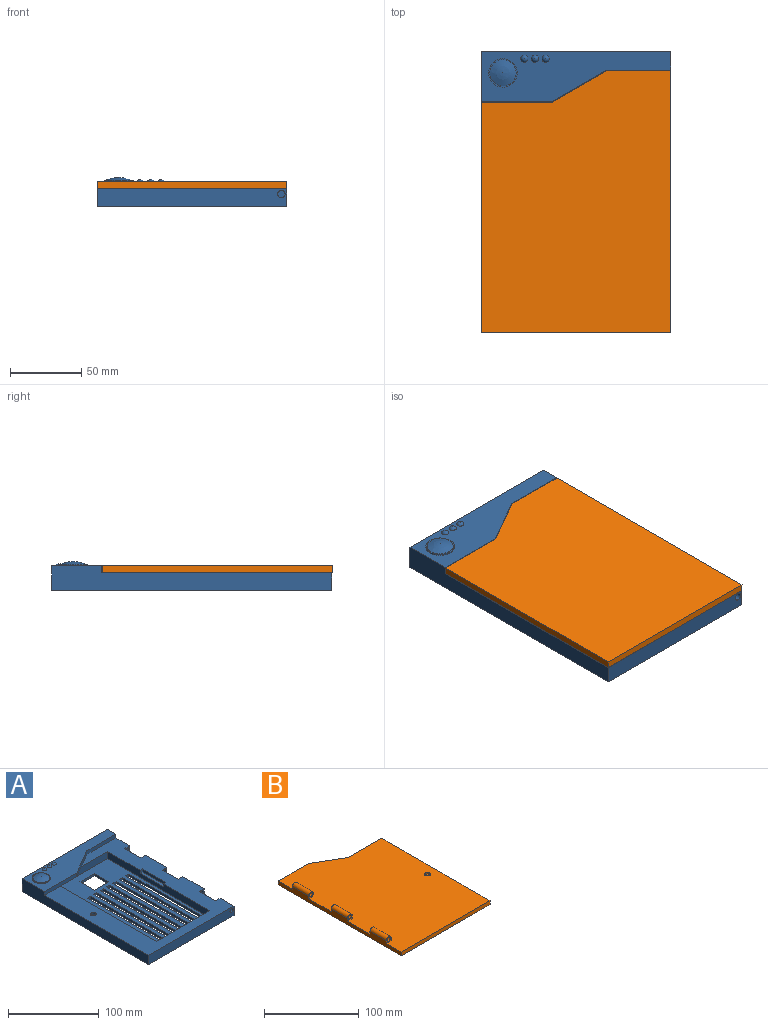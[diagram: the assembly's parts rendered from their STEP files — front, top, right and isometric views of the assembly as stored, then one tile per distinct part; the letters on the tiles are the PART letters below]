
ASSEMBLY  parts=2 mates=1
PART A: 81 faces, bbox 133x197x20.5 mm
  f0: plane 184x133mm, normal (0,0,1), area 9273.6mm2, adj f1,f2,f4,f5,f33,f45,f46,f47
  f1: plane 197x17.5mm, normal (1,0,0), area 1965mm2, adj f0,f3,f33,f44,f49,f52,f60,f61
  f2: plane 197x17.5mm, normal (-1,0,0), area 2637.5mm2, adj f0,f3,f33,f44,f50,f52
  f3: plane 133x17.5mm, normal (0,1,0), area 2327.5mm2, adj f1,f2,f44,f52
  f4: plane 159.5x9.5mm, normal (1,0,0), area 1515.3mm2, adj f0,f5,f43,f45,f53
  f5: plane 83.25x9.5mm, normal (0,-1,0), area 790.9mm2, adj f0,f4,f43,f46,f53
  f6: plane 5x3mm, normal (0,-1,0), area 15mm2, adj f7,f42,f43,f44
  f7: plane 117x3mm, normal (-1,0,0), area 351mm2, adj f6,f8,f43,f44
  f8: plane 5x3mm, normal (0,1,0), area 15mm2, adj f7,f42,f43,f44
  f9: plane 5x3mm, normal (0,-1,0), area 15mm2, adj f10,f34,f43,f44
  f10: plane 117x3mm, normal (-1,0,0), area 351mm2, adj f9,f11,f43,f44
  f11: plane 5x3mm, normal (0,1,0), area 15mm2, adj f10,f34,f43,f44
  f12: plane 5x3mm, normal (0,-1,0), area 15mm2, adj f13,f35,f43,f44
  f13: plane 117x3mm, normal (-1,0,0), area 351mm2, adj f12,f14,f43,f44
  f14: plane 5x3mm, normal (0,1,0), area 15mm2, adj f13,f35,f43,f44
  f15: plane 5x3mm, normal (0,-1,0), area 15mm2, adj f16,f36,f43,f44
  f16: plane 117x3mm, normal (-1,0,0), area 351mm2, adj f15,f17,f43,f44
  f17: plane 5x3mm, normal (0,1,0), area 15mm2, adj f16,f36,f43,f44
  f18: plane 5x3mm, normal (0,-1,0), area 15mm2, adj f19,f37,f43,f44
  f19: plane 117x3mm, normal (-1,0,0), area 351mm2, adj f18,f20,f43,f44
  f20: plane 5x3mm, normal (0,1,0), area 15mm2, adj f19,f37,f43,f44
  f21: plane 5x3mm, normal (0,-1,0), area 15mm2, adj f22,f38,f43,f44
  f22: plane 117x3mm, normal (-1,0,0), area 351mm2, adj f21,f23,f43,f44
  f23: plane 5x3mm, normal (0,1,0), area 15mm2, adj f22,f38,f43,f44
  f24: plane 5x3mm, normal (0,-1,0), area 15mm2, adj f25,f39,f43,f44
  f25: plane 117x3mm, normal (-1,0,0), area 351mm2, adj f24,f26,f43,f44
  f26: plane 5x3mm, normal (0,1,0), area 15mm2, adj f25,f39,f43,f44
  f27: plane 22.5x3mm, normal (0,1,0), area 67.5mm2, adj f28,f40,f43,f44
  f28: plane 22.5x3mm, normal (1,0,0), area 67.5mm2, adj f27,f29,f43,f44
  f29: plane 22.5x3mm, normal (0,-1,0), area 67.5mm2, adj f28,f40,f43,f44
  f30: plane 5x3mm, normal (0,1,0), area 15mm2, adj f31,f41,f43,f44
  f31: plane 117x3mm, normal (1,0,0), area 351mm2, adj f30,f32,f43,f44
  f32: plane 5x3mm, normal (0,-1,0), area 15mm2, adj f31,f41,f43,f44
  f33: plane 133x12.5mm, normal (0,-1,0), area 1640.9mm2, adj f0,f1,f2,f44,f76
  f34: plane 117x3mm, normal (1,0,0), area 351mm2, adj f9,f11,f43,f44
  f35: plane 117x3mm, normal (1,0,0), area 351mm2, adj f12,f14,f43,f44
  f36: plane 117x3mm, normal (1,0,0), area 351mm2, adj f15,f17,f43,f44
  f37: plane 117x3mm, normal (1,0,0), area 351mm2, adj f18,f20,f43,f44
  f38: plane 117x3mm, normal (1,0,0), area 351mm2, adj f21,f23,f43,f44
  f39: plane 117x3mm, normal (1,0,0), area 351mm2, adj f24,f26,f43,f44
  f40: plane 22.5x3mm, normal (-1,0,0), area 67.5mm2, adj f27,f29,f43,f44
  f41: plane 117x3mm, normal (-1,0,0), area 351mm2, adj f30,f32,f43,f44
  f42: plane 117x3mm, normal (1,0,0), area 351mm2, adj f6,f8,f43,f44
  f43: plane 159.5x83.25mm, normal (0,0,1), area 8092.1mm2, adj f4,f5,f6,f7,f8,f9,f10,f11
  f44: plane 197x133mm, normal (0,0,-1), area 21014.8mm2, adj f1,f2,f3,f6,f7,f8,f9,f10
  f45: plane 83.25x9.5mm, normal (0,1,0), area 790.9mm2, adj f0,f4,f43,f46
  f46: plane 159.5x9.5mm, normal (-1,0,0), area 1371.3mm2, adj f0,f5,f43,f45,f77,f79,f80
  f47: cylinder r=3.25mm len=6.5mm, axis (0,0,1), area 51.1mm2, adj f0,f48
  f48: plane 6.5x6.5mm, normal (0,0,1), area 33.2mm2, adj f47
  f49: plane 45x5mm, normal (0,-1,0), area 225mm2, adj f0,f1,f51,f52
  f50: plane 50x5mm, normal (0,-1,0), area 250mm2, adj f0,f2,f51,f52,f53
  f51: plane 38x22mm, normal (0.5,-0.87,0), area 219.5mm2, adj f0,f49,f50,f52,f53
  f52: plane 133x35mm, normal (0,0,1), area 2873.9mm2, adj f1,f2,f3,f49,f50,f51,f54,f57
  f53: plane 42.4x10mm, normal (0,0,-1), area 337.6mm2, adj f4,f5,f50,f51
  f54: cylinder r=10mm len=20mm, axis (0,0,-1), area 62.8mm2, adj f52,f55
  f55: plane 20x20mm, normal (0,0,1), area 48.3mm2, adj f54,f56
  f56: revolved ~18.4x18.4mm, area 277.6mm2, adj f55
  f57: sphere r=2.75mm, area 27.7mm2, adj f52
  f58: sphere r=2.75mm, area 27.7mm2, adj f52
  f59: sphere r=2.75mm, area 27.7mm2, adj f52
  f60: plane 7.5x7.5mm, normal (0,1,0), area 34.6mm2, adj f0,f1,f62,f63,f76
  f61: plane 7.5x7.5mm, normal (0,-1,0), area 34.6mm2, adj f0,f1,f62,f63,f75
  f62: plane 25x7.5mm, normal (1,0,0), area 187.5mm2, adj f0,f60,f61,f63
  f63: plane 25x7.5mm, normal (0,0,1), area 187.5mm2, adj f1,f60,f61,f62
  f64: plane 7.5x7.5mm, normal (0,1,0), area 34.6mm2, adj f0,f1,f66,f67,f75
  f65: plane 7.5x7.5mm, normal (0,-1,0), area 34.6mm2, adj f0,f1,f66,f67,f74
  f66: plane 25x7.5mm, normal (1,0,0), area 187.5mm2, adj f0,f64,f65,f67
  f67: plane 25x7.5mm, normal (0,0,1), area 187.5mm2, adj f1,f64,f65,f66
  f68: plane 7.5x7.5mm, normal (0,1,0), area 34.6mm2, adj f0,f1,f70,f71,f74
  f69: plane 7.5x7.5mm, normal (0,-1,0), area 34.6mm2, adj f0,f1,f70,f71,f73
  f70: plane 25x7.5mm, normal (1,0,0), area 187.5mm2, adj f0,f68,f69,f71
  f71: plane 25x7.5mm, normal (0,0,1), area 187.5mm2, adj f1,f68,f69,f70
  f72: plane 5.25x5.25mm, normal (0,-1,0), area 21.6mm2, adj f73
  f73: cylinder r=2.62mm len=10mm, axis (0,1,0), area 164.9mm2, adj f69,f72
  f74: cylinder r=2.62mm len=33mm, axis (0,1,0), area 544.3mm2, adj f65,f68
  f75: cylinder r=2.62mm len=33mm, axis (0,1,0), area 544.3mm2, adj f61,f64
  f76: cylinder r=2.62mm len=21.5mm, axis (0,1,0), area 354.6mm2, adj f33,f60
  f77: plane 4x4mm, normal (0,1,0), area 16mm2, adj f0,f46,f78,f80
  f78: plane 36x4mm, normal (-1,0,0), area 144mm2, adj f0,f77,f79,f80
  f79: plane 4x4mm, normal (0,-1,0), area 16mm2, adj f0,f46,f78,f80
  f80: plane 36x4mm, normal (0,0,1), area 144mm2, adj f46,f77,f78,f79
PART B: 25 faces, bbox 133x184x12 mm
  f0: plane 184x133mm, normal (0,0,1), area 22406.3mm2, adj f1,f2,f3,f4,f5,f6,f8,f9
  f1: plane 45x5mm, normal (0,1,0), area 225mm2, adj f0,f2,f6,f7
  f2: plane 184x8.5mm, normal (-1,0,0), area 1177.3mm2, adj f0,f1,f3,f7,f8,f9,f11,f12
  f3: plane 133x5mm, normal (0,-1,0), area 665mm2, adj f0,f2,f4,f7
  f4: plane 162x5mm, normal (1,0,0), area 810mm2, adj f0,f3,f5,f7
  f5: plane 50x5mm, normal (0,1,0), area 250mm2, adj f0,f4,f6,f7
  f6: plane 38x22mm, normal (0.5,0.87,0), area 219.5mm2, adj f0,f1,f5,f7
  f7: plane 184x133mm, normal (0,0,-1), area 22954mm2, adj f1,f2,f3,f4,f5,f6
  f8: plane 7x7mm, normal (0,1,0), area 22.1mm2, adj f0,f2,f10,f17,f22
  f9: plane 7x7mm, normal (0,-1,0), area 22.1mm2, adj f0,f2,f10,f17,f22
  f10: plane 24.5x3.5mm, normal (1,0,0), area 85.8mm2, adj f0,f8,f9,f17
  f11: plane 7x7mm, normal (0,1,0), area 22.1mm2, adj f0,f2,f13,f18,f21
  f12: plane 7x7mm, normal (0,-1,0), area 22.1mm2, adj f0,f2,f13,f18,f21
  f13: plane 24.5x3.5mm, normal (1,0,0), area 85.8mm2, adj f0,f11,f12,f18
  f14: plane 7x7mm, normal (0,1,0), area 22.1mm2, adj f0,f2,f16,f19,f20
  f15: plane 7x7mm, normal (0,-1,0), area 22.1mm2, adj f0,f2,f16,f19,f20
  f16: plane 24.5x3.5mm, normal (1,0,0), area 85.8mm2, adj f0,f14,f15,f19
  f17: cylinder r=3.5mm len=24.5mm, axis (0,-1,0), area 269.4mm2, adj f2,f8,f9,f10
  f18: cylinder r=3.5mm len=24.5mm, axis (0,-1,0), area 269.4mm2, adj f2,f11,f12,f13
  f19: cylinder r=3.5mm len=24.5mm, axis (0,-1,0), area 269.4mm2, adj f2,f14,f15,f16
  f20: cylinder r=2.62mm len=24.5mm, axis (0,-1,0), area 404.1mm2, adj f14,f15
  f21: cylinder r=2.62mm len=24.5mm, axis (0,-1,0), area 404.1mm2, adj f11,f12
  f22: cylinder r=2.62mm len=24.5mm, axis (0,-1,0), area 404.1mm2, adj f8,f9
  f23: cylinder r=3.25mm len=6.5mm, axis (0,0,1), area 40.8mm2, adj f0,f24
  f24: plane 6.5x6.5mm, normal (0,0,1), area 33.2mm2, adj f23
PLACE A t=(-133.14,9.39,37.19)mm
PLACE B rot(axis=(0,-1,0),180deg) t=(-157.14,-56.81,54.74)mm
MATE revolute B.f20 <-> A.f73  axis (0,-1,0) through (-81.64,-76.1,45.94)mm
